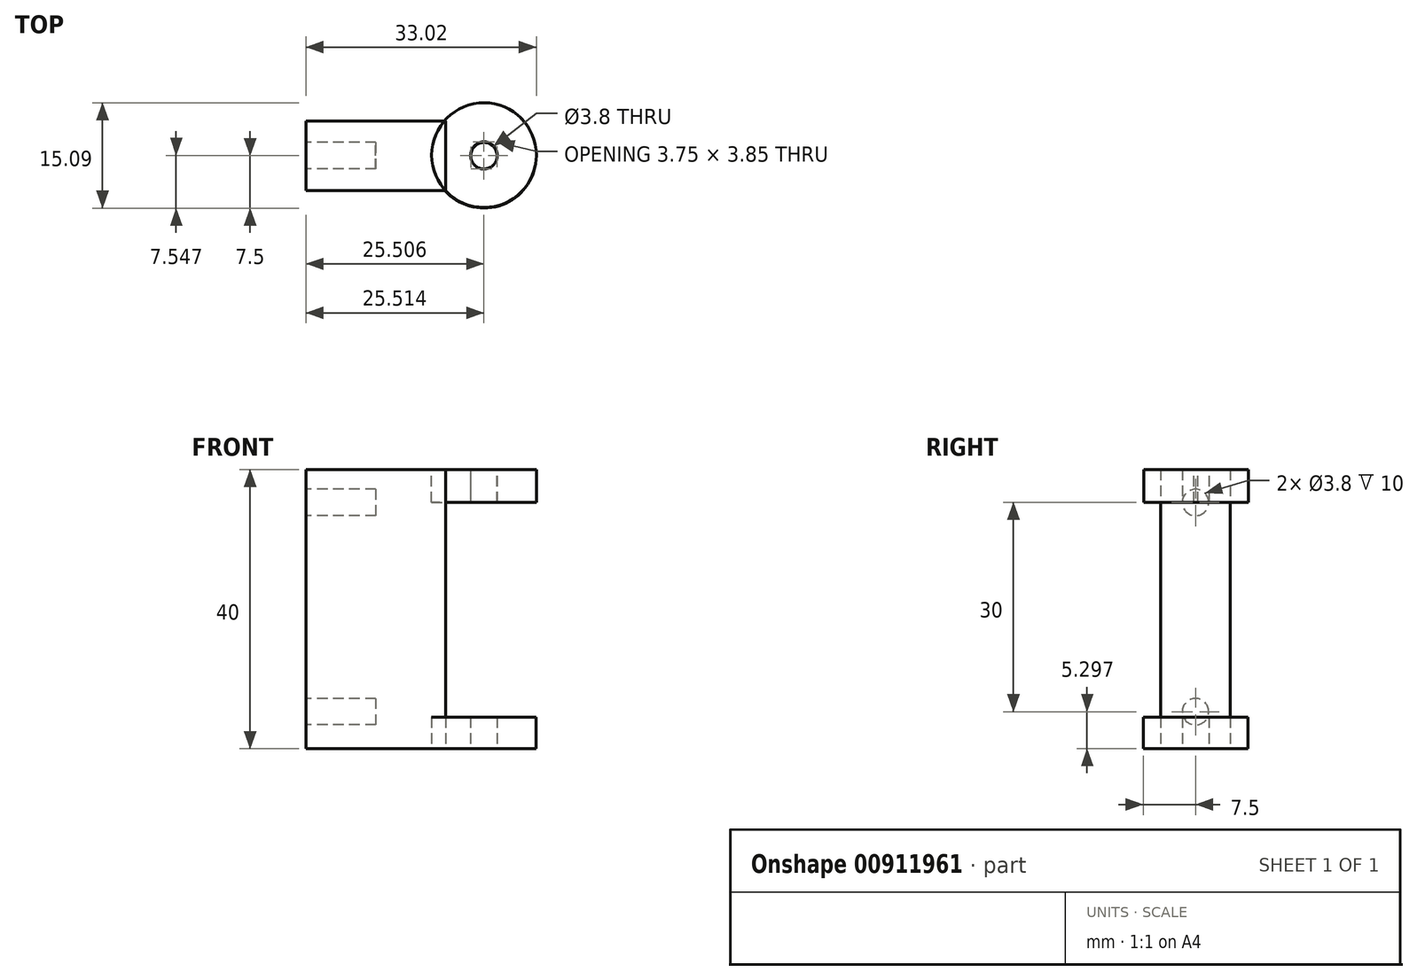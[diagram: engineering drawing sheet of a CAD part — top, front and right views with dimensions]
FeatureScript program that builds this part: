
annotation { "Feature Type Name" : "Feature", "Feature Type Description" : "" }
export const myFeature = defineFeature(function(context is Context, id is Id, definition is map)
    precondition{}
    {
        {
            var Q0;
            Q0=qCreatedBy(makeId("Front.planeOp"),FACE);
            var sketch = newSketch(context, id + "F0", { "sketchPlane" : qUnion([Q0])});
            skLineSegment(sketch, "E0.bottom", {"start": v(-57.22, 45.63) * mm, "end": v(-37.22, 45.63) * mm});
            skLineSegment(sketch, "E0.top", {"start": v(-57.22, 5.63) * mm, "end": v(-37.22, 5.63) * mm});
            skLineSegment(sketch, "E0.left", {"start": v(-57.22, 45.63) * mm, "end": v(-57.22, 5.63) * mm});
            skLineSegment(sketch, "E0.right", {"start": v(-37.22, 45.63) * mm, "end": v(-37.22, 5.63) * mm});
            skSolve(sketch);
        }
        {
            var Q0;
            Q0 = qSketchRegion(id + "F0", true);
            extrude(context, id + "F1", {"entities" : qUnion([Q0]), "depth" : 10 * mm, "offsetDistance" : 25 * mm});
        }
        {
            var Q0;
            Q0=makeQuery(id+"F1.opExtrude","SWEPT_FACE",FACE,{"disambiguationData":[OSD([sQuery(id+"F0.wireOp",EDGE,"E0.bottom")])]});
            var sketch = newSketch(context, id + "F2", { "sketchPlane" : qUnion([Q0])});
            skCircle(sketch, "E1", {"center": v(-31.7, -4.9) * mm, "radius": 7.5 * mm});
            skSolve(sketch);
        }
        {
            var Q0;
            Q0 = qSketchRegion(id + "F2", true);
            extrude(context, id + "F3", {"entities" : qUnion([Q0]), "oppositeDirection" : true, "depth" : 4.7 * mm, "offsetDistance" : 25 * mm});
        }
        {
            var Q0;
            Q0=makeQuery(id+"F1.opExtrude","SWEPT_FACE",FACE,{"disambiguationData":[OSD([sQuery(id+"F0.wireOp",EDGE,"E0.top")])]});
            var sketch = newSketch(context, id + "F4", { "sketchPlane" : qUnion([Q0])});
            skCircle(sketch, "E2", {"center": v(-31.71, 5) * mm, "radius": 7.5 * mm});
            skPoint(sketch, "E3", {"position": v(-37.22, 5) * mm});
            skSolve(sketch);
        }
        {
            var Q0;
            Q0 = qSketchRegion(id + "F4", true);
            extrude(context, id + "F5", {"entities" : qUnion([Q0]), "oppositeDirection" : true, "depth" : 4.5 * mm, "offsetDistance" : 25 * mm});
        }
        {
            var Q0;
            Q0=makeQuery(id+"F5.opExtrude","CAP_FACE",FACE,{"disambiguationData":[OSD([sQuery(id+"F4.wireOp",EDGE,"E2")])],"isStart":true});
            var sketch = newSketch(context, id + "F6", { "sketchPlane" : qUnion([Q0])});
            skCircle(sketch, "E4", {"center": v(-31.71, 5) * mm, "radius": 1.9 * mm});
            skSolve(sketch);
        }
        {
            var Q0;
            Q0 = qSketchRegion(id + "F6", true);
            extrude(context, id + "F7", {"entities" : qUnion([Q0]), "operationType" : NewBodyOperationType.REMOVE, "oppositeDirection" : true, "depth" : 60 * mm, "offsetDistance" : 25 * mm});
        }
        {
            var Q0;
            Q0=makeQuery(id+"F3.opExtrude","CAP_FACE",FACE,{"disambiguationData":[OSD([sQuery(id+"F2.wireOp",EDGE,"E1")])],"isStart":true});
            var sketch = newSketch(context, id + "F8", { "sketchPlane" : qUnion([Q0])});
            skCircle(sketch, "E5", {"center": v(-31.7, -4.9) * mm, "radius": 1.9 * mm});
            skSolve(sketch);
        }
        {
            var Q0;
            Q0 = qSketchRegion(id + "F8", true);
            extrude(context, id + "F9", {"entities" : qUnion([Q0]), "operationType" : NewBodyOperationType.REMOVE, "oppositeDirection" : true, "depth" : 25 * mm, "offsetDistance" : 25 * mm});
        }
        {
            var Q0;
            Q0=makeQuery(id+"F1.opExtrude","SWEPT_FACE",FACE,{"disambiguationData":[OSD([sQuery(id+"F0.wireOp",EDGE,"E0.left")])]});
            var sketch = newSketch(context, id + "F10", { "sketchPlane" : qUnion([Q0])});
            skCircle(sketch, "E6", {"center": v(5, 40.93) * mm, "radius": 1.9 * mm});
            skPoint(sketch, "E6.centerSnap0", {"position": v(5, 45.63) * mm});
            skCircle(sketch, "E7", {"center": v(5, 10.93) * mm, "radius": 1.9 * mm});
            skPoint(sketch, "E7.centerSnap0", {"position": v(5, 5.63) * mm});
            skSolve(sketch);
        }
        {
            var Q0;
            Q0 = qSketchRegion(id + "F10", true);
            extrude(context, id + "F11", {"entities" : qUnion([Q0]), "operationType" : NewBodyOperationType.REMOVE, "oppositeDirection" : true, "depth" : 10 * mm, "offsetDistance" : 25 * mm});
        }
    });
